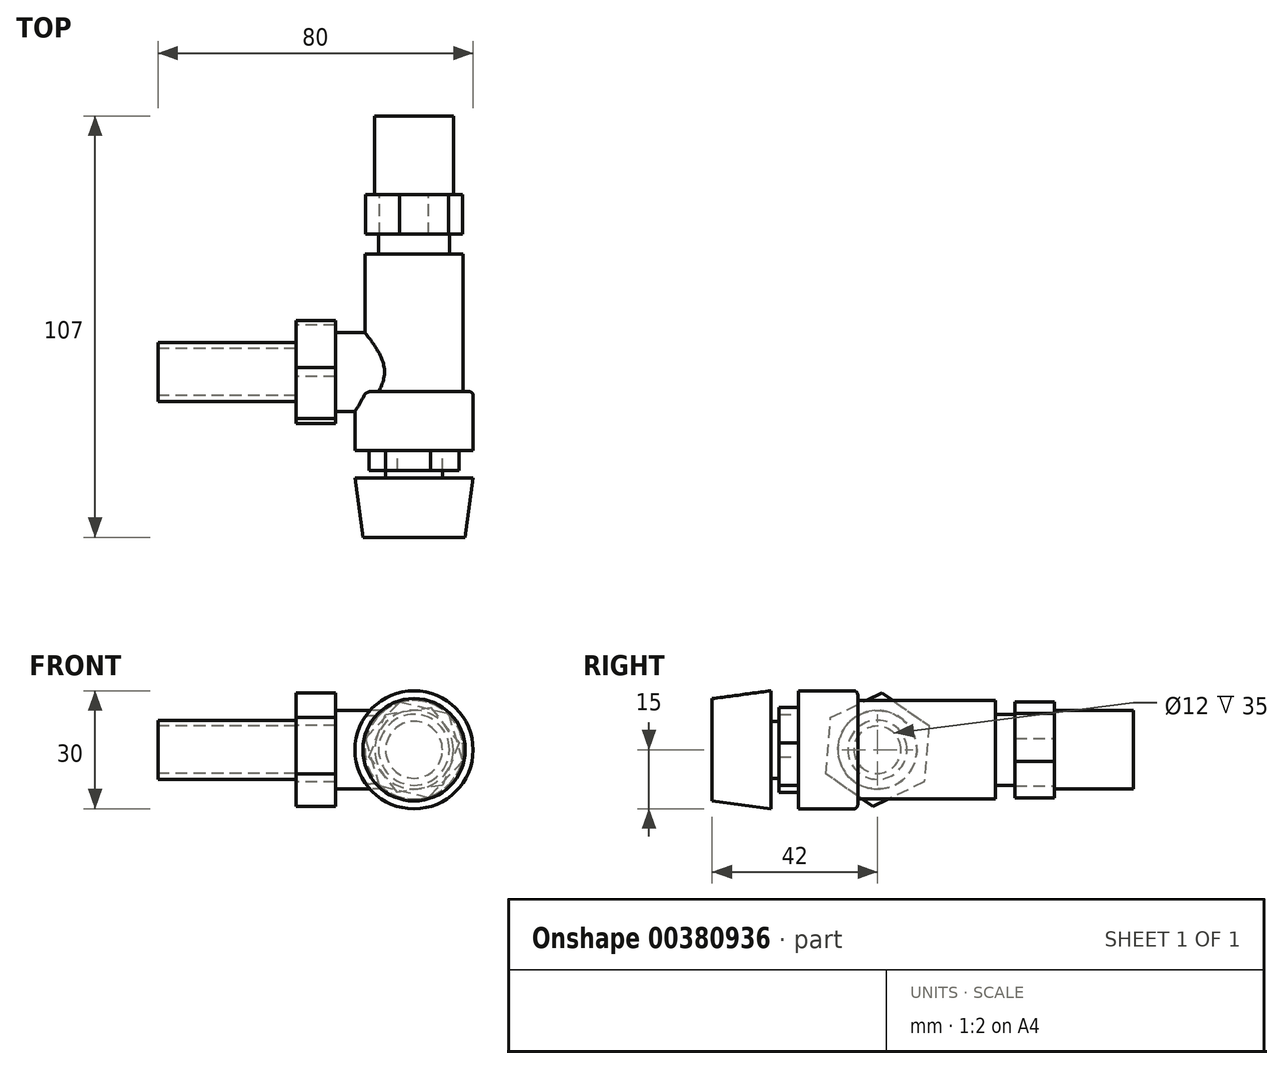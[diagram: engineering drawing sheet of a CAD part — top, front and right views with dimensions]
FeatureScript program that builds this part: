
annotation { "Feature Type Name" : "Feature", "Feature Type Description" : "" }
export const myFeature = defineFeature(function(context is Context, id is Id, definition is map)
    precondition{}
    {
        {
            var Q0;
            Q0=qCreatedBy(makeId("Front.planeOp"),FACE);
            var sketch = newSketch(context, id + "F0", { "sketchPlane" : qUnion([Q0])});
            skCircle(sketch, "E0", {"center": v(0, 0) * mm, "radius": 10 * mm});
            skSolve(sketch);
        }
        {
            var Q0;
            Q0 = qSketchRegion(id + "F0", true);
            extrude(context, id + "F1", {"entities" : qUnion([Q0]), "endBound" : BoundingType.SYMMETRIC, "depth" : 20 * mm});
        }
        {
            var Q0;
            Q0=makeQuery(id+"F1.opExtrude","CAP_FACE",FACE,{"disambiguationData":[OSD([sQuery(id+"F0.wireOp",EDGE,"E0")])],"isStart":false});
            var sketch = newSketch(context, id + "F2", { "sketchPlane" : qUnion([Q0])});
            skCircle(sketch, "E1.cCircle", {"center": v(0, 0) * mm, "radius": 11 * mm, "construction": true});
            skLineSegment(sketch, "E1.0", {"start": v(12.36, -2.94) * mm, "end": v(3.64, -12.17) * mm});
            skLineSegment(sketch, "E1.1", {"start": v(3.64, -12.17) * mm, "end": v(-8.72, -9.23) * mm});
            skLineSegment(sketch, "E1.2", {"start": v(-8.72, -9.23) * mm, "end": v(-12.36, 2.94) * mm});
            skLineSegment(sketch, "E1.3", {"start": v(-12.36, 2.94) * mm, "end": v(-3.64, 12.17) * mm});
            skLineSegment(sketch, "E1.4", {"start": v(-3.64, 12.17) * mm, "end": v(8.72, 9.23) * mm});
            skLineSegment(sketch, "E1.5", {"start": v(8.72, 9.23) * mm, "end": v(12.36, -2.94) * mm});
            skPoint(sketch, "E1.0.midPoint", {"position": v(8, -7.55) * mm});
            skSolve(sketch);
        }
        {
            var Q0;
            Q0 = qSketchRegion(id + "F2", true);
            extrude(context, id + "F3", {"entities" : qUnion([Q0]), "operationType" : NewBodyOperationType.ADD, "depth" : 10 * mm});
        }
        {
            var Q0;
            Q0=makeQuery(id+"F3.opExtrude","CAP_FACE",FACE,{"disambiguationData":[OSD([sQuery(id+"F2.wireOp",EDGE,"E1.0"),sQuery(id+"F2.wireOp",EDGE,"E1.1"),sQuery(id+"F2.wireOp",EDGE,"E1.2"),sQuery(id+"F2.wireOp",EDGE,"E1.3"),sQuery(id+"F2.wireOp",EDGE,"E1.4"),sQuery(id+"F2.wireOp",EDGE,"E1.5")])],"isStart":false});
            var sketch = newSketch(context, id + "F4", { "sketchPlane" : qUnion([Q0])});
            skCircle(sketch, "E2", {"center": v(0, 0) * mm, "radius": 9 * mm});
            skSolve(sketch);
        }
        {
            var Q0;
            Q0 = qSketchRegion(id + "F4", true);
            extrude(context, id + "F5", {"entities" : qUnion([Q0]), "operationType" : NewBodyOperationType.ADD, "depth" : 5 * mm});
        }
        {
            var Q0;
            Q0=makeQuery(id+"F5.opExtrude","CAP_FACE",FACE,{"disambiguationData":[OSD([sQuery(id+"F4.wireOp",EDGE,"E2")])],"isStart":false});
            var sketch = newSketch(context, id + "F6", { "sketchPlane" : qUnion([Q0])});
            skCircle(sketch, "E3", {"center": v(0, 0) * mm, "radius": 12.5 * mm});
            skSolve(sketch);
        }
        {
            var Q0;
            Q0 = qSketchRegion(id + "F6", true);
            extrude(context, id + "F7", {"entities" : qUnion([Q0]), "operationType" : NewBodyOperationType.ADD, "depth" : 35 * mm});
        }
        {
            var Q0;
            Q0=makeQuery(id+"F7.opExtrude","CAP_FACE",FACE,{"disambiguationData":[OSD([sQuery(id+"F6.wireOp",EDGE,"E3")])],"isStart":false});
            var sketch = newSketch(context, id + "F8", { "sketchPlane" : qUnion([Q0])});
            skCircle(sketch, "E4", {"center": v(0, 0) * mm, "radius": 15 * mm});
            skSolve(sketch);
        }
        {
            var Q0;
            Q0 = qSketchRegion(id + "F8", true);
            extrude(context, id + "F9", {"entities" : qUnion([Q0]), "operationType" : NewBodyOperationType.ADD, "depth" : 15 * mm});
        }
        {
            var Q0;
            Q0=makeQuery(id+"F9.opExtrude","CAP_EDGE",EDGE,{"disambiguationData":[OSD([sQuery(id+"F8.wireOp",EDGE,"E4")])],"isStart":true});
            var Q1;
            Q1=makeQuery(id+"F7.opExtrude","CAP_EDGE",EDGE,{"disambiguationData":[OSD([sQuery(id+"F6.wireOp",EDGE,"E3")])],"isStart":false});
            fillet(context, id + "F10", {"entities" : qUnion([Q0, Q1]), "radius" : 1 * mm, "tangentPropagation" : true, "allowEdgeOverflow" : false});
        }
        {
            var Q0;
            Q0=makeQuery(id+"F9.opExtrude","CAP_FACE",FACE,{"disambiguationData":[OSD([sQuery(id+"F8.wireOp",EDGE,"E4")])],"isStart":false});
            var sketch = newSketch(context, id + "F11", { "sketchPlane" : qUnion([Q0])});
            skCircle(sketch, "E5.cCircle", {"center": v(0, 0) * mm, "radius": 10 * mm, "construction": true});
            skLineSegment(sketch, "E5.0", {"start": v(11.41, 1.77) * mm, "end": v(7.24, -9) * mm});
            skLineSegment(sketch, "E5.1", {"start": v(7.24, -9) * mm, "end": v(-4.17, -10.77) * mm});
            skLineSegment(sketch, "E5.2", {"start": v(-4.17, -10.77) * mm, "end": v(-11.41, -1.77) * mm});
            skLineSegment(sketch, "E5.3", {"start": v(-11.41, -1.77) * mm, "end": v(-7.24, 9) * mm});
            skLineSegment(sketch, "E5.4", {"start": v(-7.24, 9) * mm, "end": v(4.17, 10.77) * mm});
            skLineSegment(sketch, "E5.5", {"start": v(4.17, 10.77) * mm, "end": v(11.41, 1.77) * mm});
            skPoint(sketch, "E5.0.midPoint", {"position": v(9.32, -3.61) * mm});
            skSolve(sketch);
        }
        {
            var Q0;
            Q0 = qSketchRegion(id + "F11", true);
            extrude(context, id + "F12", {"entities" : qUnion([Q0]), "operationType" : NewBodyOperationType.ADD, "depth" : 5 * mm});
        }
        {
            var Q0;
            Q0=makeQuery(id+"F12.opExtrude","CAP_FACE",FACE,{"disambiguationData":[OSD([sQuery(id+"F11.wireOp",EDGE,"E5.0"),sQuery(id+"F11.wireOp",EDGE,"E5.1"),sQuery(id+"F11.wireOp",EDGE,"E5.2"),sQuery(id+"F11.wireOp",EDGE,"E5.3"),sQuery(id+"F11.wireOp",EDGE,"E5.4"),sQuery(id+"F11.wireOp",EDGE,"E5.5")])],"isStart":false});
            var sketch = newSketch(context, id + "F13", { "sketchPlane" : qUnion([Q0])});
            skCircle(sketch, "E6", {"center": v(0, 0) * mm, "radius": 7.21 * mm});
            skSolve(sketch);
        }
        {
            var Q0;
            Q0 = qSketchRegion(id + "F13", true);
            extrude(context, id + "F14", {"entities" : qUnion([Q0]), "operationType" : NewBodyOperationType.ADD, "depth" : 2 * mm});
        }
        {
            var Q0;
            Q0=qCreatedBy(makeId("Right.planeOp"),FACE);
            var sketch = newSketch(context, id + "F15", { "sketchPlane" : qUnion([Q0])});
            skLineSegment(sketch, "E7", {"start": v(0, 0) * mm, "end": v(-82, 0) * mm, "construction": true});
            skLineSegment(sketch, "E8.0", {"start": v(-82, -7.21) * mm, "end": v(-82, 7.21) * mm});
            skLineSegment(sketch, "E9", {"start": v(-82, 0) * mm, "end": v(-82, 15) * mm});
            skLineSegment(sketch, "E10", {"start": v(-82, 15) * mm, "end": v(-97, 13) * mm});
            skLineSegment(sketch, "E11", {"start": v(-97, 13) * mm, "end": v(-97, 0) * mm});
            skLineSegment(sketch, "E12", {"start": v(-97, 0) * mm, "end": v(-82, 0) * mm});
            skSolve(sketch);
        }
        {
            var Q0;
            Q0 = qSketchRegion(id + "F15", true);
            var Q1;
            Q1=sQuery(id+"F15.wireOp",EDGE,"E7");
            revolve(context, id + "F16", {"operationType" : NewBodyOperationType.ADD, "entities" : qUnion([Q0]), "axis" : qUnion([Q1]), "revolveType" : RevolveType.FULL});
        }
        {
            var Q0;
            Q0=qCreatedBy(makeId("Front.planeOp"),FACE);
            cPlane(context, id + "F17", {"entities" : qUnion([Q0]), "cplaneType" : CPlaneType.OFFSET, "offset" : 55 * mm, "width" : 152.4 * mm, "height" : 152.4 * mm});
        }
        {
            var Q0;
            Q0=qCreatedBy(makeId("Right.planeOp"),FACE);
            cPlane(context, id + "F18", {"entities" : qUnion([Q0]), "cplaneType" : CPlaneType.OFFSET, "offset" : 65 * mm, "oppositeDirection" : true, "width" : 152.4 * mm, "height" : 152.4 * mm});
        }
        {
            var Q0;
            Q0=qCreatedBy(id+"F18.planeOp",FACE);
            var sketch = newSketch(context, id + "F19", { "sketchPlane" : qUnion([Q0])});
            skCircle(sketch, "E13", {"center": v(-55, 0) * mm, "radius": 7.5 * mm});
            skCircle(sketch, "E14", {"center": v(-55, 0) * mm, "radius": 6 * mm});
            skSolve(sketch);
        }
        {
            var Q0;
            Q0 = qSketchRegion(id + "F19", true);
            var Q1;
            Q1=makeQuery(id+"F19.imprint","IMPRINT",FACE,{"disambiguationData":[TD([[makeQuery(id+"F19.imprint","IMPRINT",EDGE,{"derivedFrom":sQuery(id+"F19.wireOp",EDGE,"E13")}),1.0]])]});
            extrude(context, id + "F20", {"entities" : qUnion([Q0, Q1]), "operationType" : NewBodyOperationType.ADD, "endBound" : BoundingType.UP_TO_NEXT, "depth" : 25.4 * mm});
        }
        {
            var Q0;
            Q0=qCreatedBy(makeId("Right.planeOp"),FACE);
            cPlane(context, id + "F21", {"entities" : qUnion([Q0]), "cplaneType" : CPlaneType.OFFSET, "offset" : 30 * mm, "oppositeDirection" : true, "width" : 152.4 * mm, "height" : 152.4 * mm});
        }
        {
            var Q0;
            Q0=qCreatedBy(id+"F21.planeOp",FACE);
            var sketch = newSketch(context, id + "F22", { "sketchPlane" : qUnion([Q0])});
            skCircle(sketch, "E15.cCircle", {"center": v(-55, 0) * mm, "radius": 12.5 * mm, "construction": true});
            skLineSegment(sketch, "E15.0", {"start": v(-56.18, -14.39) * mm, "end": v(-68.05, -6.17) * mm});
            skLineSegment(sketch, "E15.1", {"start": v(-68.05, -6.17) * mm, "end": v(-66.87, 8.21) * mm});
            skLineSegment(sketch, "E15.2", {"start": v(-66.87, 8.21) * mm, "end": v(-53.82, 14.39) * mm});
            skLineSegment(sketch, "E15.3", {"start": v(-53.82, 14.39) * mm, "end": v(-41.95, 6.17) * mm});
            skLineSegment(sketch, "E15.4", {"start": v(-41.95, 6.17) * mm, "end": v(-43.13, -8.21) * mm});
            skLineSegment(sketch, "E15.5", {"start": v(-43.13, -8.21) * mm, "end": v(-56.18, -14.39) * mm});
            skPoint(sketch, "E15.0.midPoint", {"position": v(-62.11, -10.28) * mm});
            skSolve(sketch);
        }
        {
            var Q0;
            Q0 = qSketchRegion(id + "F22", true);
            extrude(context, id + "F23", {"entities" : qUnion([Q0]), "operationType" : NewBodyOperationType.ADD, "depth" : 10 * mm});
        }
        {
            var Q0;
            {var subQ0=sQuery(id+"F22.wireOp",EDGE,"E15.2");var subQ1=sQuery(id+"F22.wireOp",EDGE,"E15.1");var subQ2=sQuery(id+"F22.wireOp",EDGE,"E15.0");var subQ3=sQuery(id+"F22.wireOp",EDGE,"E15.3");var subQ4=sQuery(id+"F22.wireOp",EDGE,"E15.4");var subQ5=sQuery(id+"F22.wireOp",EDGE,"E15.5");Q0=makeQuery(id+"F23.boolean.opBoolean","SPLIT",FACE,{"disambiguationData":[TD([makeQuery(id+"F20.opExtrude","SWEPT_FACE",FACE,{"disambiguationData":[OSD([sQuery(id+"F19.wireOp",EDGE,"E13")])]})])],"derivedFrom":makeQuery(id+"F23.opExtrude","CAP_FACE",FACE,{"disambiguationData":[OSD([subQ2,subQ1,subQ0,subQ3,subQ4,subQ5])],"isStart":false})});}
            var sketch = newSketch(context, id + "F24", { "sketchPlane" : qUnion([Q0])});
            skCircle(sketch, "E16", {"center": v(-55, 0) * mm, "radius": 10 * mm});
            skSolve(sketch);
        }
        {
            var Q0;
            Q0 = qSketchRegion(id + "F24", true);
            extrude(context, id + "F25", {"entities" : qUnion([Q0]), "operationType" : NewBodyOperationType.ADD, "depth" : 15 * mm});
        }
    });
